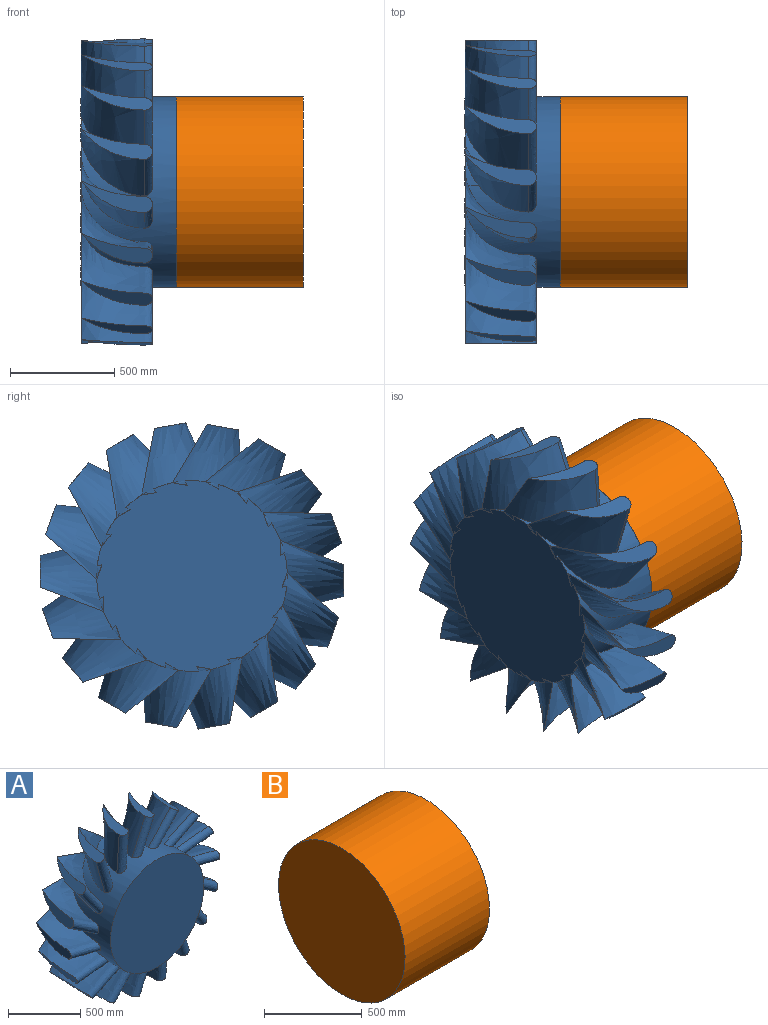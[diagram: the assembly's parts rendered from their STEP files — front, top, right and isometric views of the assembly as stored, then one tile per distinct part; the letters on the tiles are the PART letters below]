
ASSEMBLY  parts=2 mates=1
PART A: 76 faces, bbox 1457.6x459.8x1468.6 mm
  f0: plane 914.78x914.21mm, normal (0,1,0), area 643276.8mm2, adj f1,f2,f5,f6,f10,f11,f14,f15
  f1: plane 71.97x2.16mm, normal (-1,0,0), area 101.6mm2, adj f0,f2
  f2: bspline ~342.9x307.02mm, area 123612.1mm2, adj f0,f1,f3,f4,f5
  f3: bspline ~342.96x342.9mm, area 138300.3mm2, adj f2,f4,f5
  f4: plane 342.9x152.4mm, normal (1,0,0), area 19069.5mm2, adj f2,f3
  f5: cylinder r=457.2mm len=914.4mm, axis (0,1,0), area 832613.8mm2, adj f0,f2,f3,f6,f7,f9,f10,f13
  f6: cylinder r=457.2mm len=153.95mm, axis (0,1,0), area 3347.1mm2, adj f0,f5,f34,f50
  f7: plane 914.4x914.4mm, normal (0,-1,0), area 656692.9mm2, adj f5
  f8: plane 342.9x116.75mm, normal (0.77,0,-0.64), area 19069.5mm2, adj f9,f10
  f9: bspline ~404.92x371.04mm, area 138300.3mm2, adj f5,f8,f10
  f10: bspline ~404.92x371.04mm, area 123612.1mm2, adj f0,f5,f8,f9,f11
  f11: plane 55.13x46.26mm, normal (-0.77,0,0.64), area 101.6mm2, adj f0,f10
  f12: plane 342.9x150.09mm, normal (0.17,0,-0.98), area 19069.5mm2, adj f13,f14
  f13: bspline ~342.96x339.87mm, area 138300.3mm2, adj f5,f12,f14
  f14: bspline ~339.87x337.69mm, area 123612.1mm2, adj f0,f5,f12,f13,f15
  f15: plane 70.87x12.5mm, normal (-0.17,0,0.98), area 101.6mm2, adj f0,f14
  f16: plane 342.9x131.98mm, normal (-0.5,0,-0.87), area 19069.5mm2, adj f17,f18
  f17: bspline ~397.31x350.37mm, area 138300.3mm2, adj f5,f16,f18
  f18: bspline ~397.31x350.37mm, area 123612.1mm2, adj f0,f5,f16,f17,f19
  f19: plane 62.33x35.98mm, normal (0.5,0,0.87), area 101.6mm2, adj f0,f18
  f20: plane 342.9x143.21mm, normal (-0.94,0,-0.34), area 19069.5mm2, adj f21,f22
  f21: bspline ~364.6x354.86mm, area 138300.3mm2, adj f5,f20,f22
  f22: bspline ~364.6x354.86mm, area 123612.1mm2, adj f0,f5,f20,f21,f23
  f23: plane 67.63x24.62mm, normal (0.94,0,0.34), area 101.6mm2, adj f0,f22
  f24: plane 342.9x143.21mm, normal (-0.94,0,0.34), area 19069.5mm2, adj f25,f26
  f25: bspline ~377.64x342.96mm, area 138300.3mm2, adj f5,f24,f26
  f26: bspline ~377.64x322.22mm, area 123612.1mm2, adj f0,f5,f24,f25,f27
  f27: plane 67.63x24.62mm, normal (0.94,0,-0.34), area 101.6mm2, adj f0,f26
  f28: plane 342.9x131.98mm, normal (-0.5,0,0.87), area 19069.5mm2, adj f29,f30
  f29: bspline ~383.37x378.26mm, area 138300.3mm2, adj f5,f28,f30
  f30: bspline ~383.37x378.26mm, area 123612.1mm2, adj f0,f5,f28,f29,f31
  f31: plane 62.33x35.98mm, normal (0.5,0,-0.87), area 101.6mm2, adj f0,f30
  f32: plane 342.9x150.09mm, normal (0.17,0,0.98), area 19069.5mm2, adj f33,f34
  f33: bspline ~346.48x342.96mm, area 138297.4mm2, adj f5,f32,f34
  f34: bspline ~346.48x337.69mm, area 123612.6mm2, adj f0,f5,f6,f32,f33,f35
  f35: plane 70.87x12.5mm, normal (-0.17,0,-0.98), area 101.6mm2, adj f0,f34
  f36: plane 342.9x116.75mm, normal (0.77,0,0.64), area 19069.5mm2, adj f37,f38
  f37: bspline ~400.23x380.43mm, area 138300.3mm2, adj f5,f36,f38
  f38: bspline ~400.23x380.43mm, area 123612.1mm2, adj f0,f5,f36,f37,f39
  f39: plane 55.13x46.26mm, normal (-0.77,0,-0.64), area 101.6mm2, adj f0,f38
  f40: plane 342.9x143.21mm, normal (0.94,0,0.34), area 19069.5mm2, adj f41,f42
  f41: bspline ~364.6x354.86mm, area 123612.1mm2, adj f0,f5,f40,f42,f43
  f42: bspline ~364.6x354.86mm, area 138300.3mm2, adj f5,f40,f41
  f43: plane 67.63x24.62mm, normal (-0.94,0,-0.34), area 101.6mm2, adj f0,f41
  f44: plane 342.9x131.98mm, normal (0.5,0,0.87), area 19069.5mm2, adj f45,f46
  f45: bspline ~397.31x350.37mm, area 123612.1mm2, adj f0,f5,f44,f46,f47
  f46: bspline ~397.31x350.37mm, area 138300.3mm2, adj f5,f44,f45
  f47: plane 62.33x35.98mm, normal (-0.5,0,-0.87), area 101.6mm2, adj f0,f45
  f48: plane 342.9x150.09mm, normal (-0.17,0,0.98), area 19069.5mm2, adj f49,f50
  f49: bspline ~339.87x337.69mm, area 123612.1mm2, adj f0,f5,f48,f50,f51
  f50: bspline ~342.96x339.87mm, area 138290.1mm2, adj f5,f6,f48,f49
  f51: plane 70.87x12.5mm, normal (0.17,0,-0.98), area 101.6mm2, adj f0,f49
  f52: plane 342.9x116.75mm, normal (-0.77,0,0.64), area 19069.5mm2, adj f53,f54
  f53: bspline ~404.92x371.04mm, area 123612.1mm2, adj f0,f5,f52,f54,f55
  f54: bspline ~404.92x371.04mm, area 138300.3mm2, adj f5,f52,f53
  f55: plane 55.13x46.26mm, normal (0.77,0,-0.64), area 101.6mm2, adj f0,f53
  f56: plane 342.9x152.4mm, normal (-1,0,0), area 19069.5mm2, adj f57,f58
  f57: bspline ~342.9x306.89mm, area 123612.1mm2, adj f0,f5,f56,f58,f59
  f58: bspline ~342.96x342.9mm, area 138300.3mm2, adj f5,f56,f57
  f59: plane 71.97x2.16mm, normal (1,0,0), area 101.6mm2, adj f0,f57
  f60: plane 342.9x116.75mm, normal (-0.77,0,-0.64), area 19069.5mm2, adj f61,f62
  f61: bspline ~400.23x380.43mm, area 123612.1mm2, adj f0,f5,f60,f62,f63
  f62: bspline ~400.23x380.43mm, area 138300.3mm2, adj f5,f60,f61
  f63: plane 55.13x46.26mm, normal (0.77,0,0.64), area 101.6mm2, adj f0,f61
  f64: plane 342.9x150.09mm, normal (-0.17,0,-0.98), area 19069.5mm2, adj f65,f66
  f65: bspline ~346.48x337.69mm, area 123612.1mm2, adj f0,f5,f64,f66,f67
  f66: bspline ~346.48x342.96mm, area 138300.3mm2, adj f5,f64,f65
  f67: plane 70.87x12.5mm, normal (0.17,0,0.98), area 101.6mm2, adj f0,f65
  f68: plane 342.9x131.98mm, normal (0.5,0,-0.87), area 19069.5mm2, adj f69,f70
  f69: bspline ~383.37x378.26mm, area 123612.1mm2, adj f0,f5,f68,f70,f71
  f70: bspline ~383.37x378.26mm, area 138300.3mm2, adj f5,f68,f69
  f71: plane 62.33x35.98mm, normal (-0.5,0,0.87), area 101.6mm2, adj f0,f69
  f72: plane 67.63x24.62mm, normal (-0.94,0,0.34), area 101.6mm2, adj f0,f73
  f73: bspline ~377.64x322.22mm, area 123612.1mm2, adj f0,f5,f72,f74,f75
  f74: bspline ~377.64x342.96mm, area 138300.3mm2, adj f5,f73,f75
  f75: plane 342.9x143.21mm, normal (0.94,0,-0.34), area 19069.5mm2, adj f73,f74
PART B: 3 faces, bbox 609.6x914.4x914.4 mm
  f0: cylinder r=457.2mm len=914.4mm, axis (-1,0,0), area 1751181mm2, adj f1,f2
  f1: plane 914.4x914.4mm, normal (1,0,0), area 656692.9mm2, adj f0
  f2: plane 914.4x914.4mm, normal (-1,0,0), area 656692.9mm2, adj f0
PLACE A rot(axis=(0,0,1),90deg) t=(123.53,483.25,396.16)mm
PLACE B t=(352.13,59.62,337.5)mm fixed
MATE revolute A.f5 <-> B.f0  axis (1,0,0) through (352.13,59.62,337.5)mm
